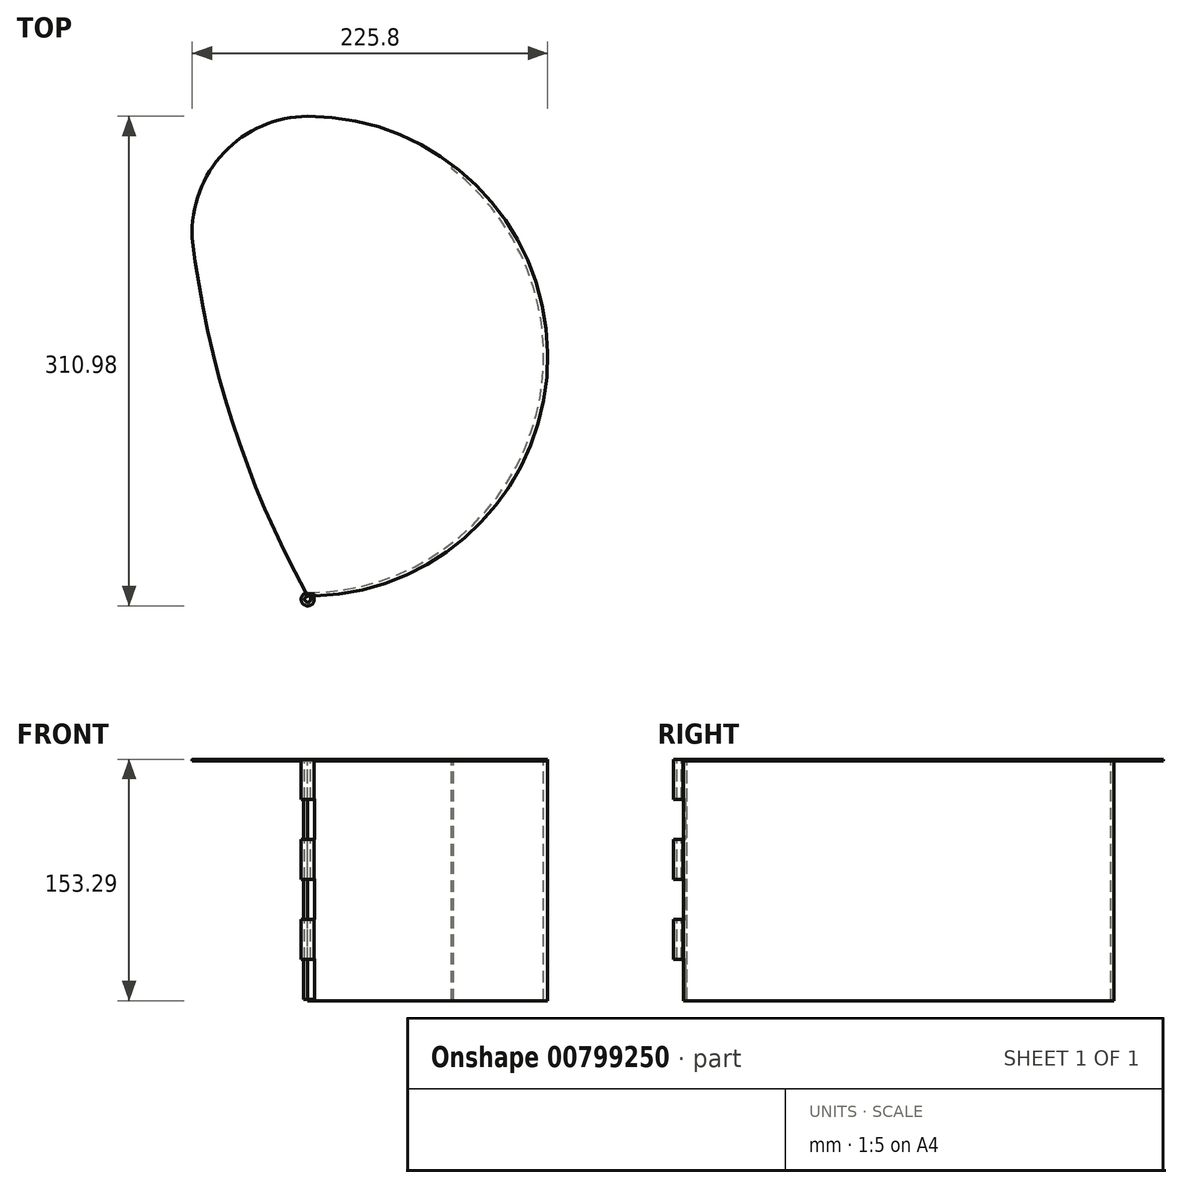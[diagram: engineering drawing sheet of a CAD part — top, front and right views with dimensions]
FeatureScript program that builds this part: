
annotation { "Feature Type Name" : "Feature", "Feature Type Description" : "" }
export const myFeature = defineFeature(function(context is Context, id is Id, definition is map)
    precondition{}
    {
        {
            var Q0;
            Q0=qCreatedBy(makeId("Top.planeOp"),FACE);
            var sketch = newSketch(context, id + "F0", { "sketchPlane" : qUnion([Q0])});
            skArc(sketch, "E0", {"start": v(-1.65, -152.87) * mm, "mid": v(150.75, -0.47) * mm, "end": v(-1.65, 151.93) * mm});
            skArc(sketch, "E1", {"start": v(-1.65, 151.93) * mm, "mid": v(-54.83, 128.83) * mm, "end": v(-74.97, 74.46) * mm});
            skArc(sketch, "E2", {"start": v(-74.97, 74.46) * mm, "mid": v(-49.39, -42.78) * mm, "end": v(-1.65, -152.87) * mm});
            skLineSegment(sketch, "E3", {"start": v(104.86, 103.41) * mm, "end": v(107.44, 105.95) * mm});
            skArc(sketch, "E4", {"start": v(-3.82, -148.92) * mm, "mid": v(134.5, -58.93) * mm, "end": v(104.86, 103.41) * mm});
            skSolve(sketch);
        }
        {
            var Q0;
            {var subQ2=sQuery(id+"F0.wireOp",EDGE,"E1");Q0=makeQuery(id+"F0.imprint","IMPRINT",FACE,{"disambiguationData":[TD([[makeQuery(id+"F0.imprint","IMPRINT",EDGE,{"derivedFrom":subQ2}),1.0]])]});}
            var Q1;
            {var subQ3=sQuery(id+"F0.wireOp",EDGE,"E3");Q1=makeQuery(id+"F0.imprint","IMPRINT",FACE,{"disambiguationData":[TD([[makeQuery(id+"F0.imprint","IMPRINT",EDGE,{"derivedFrom":subQ3}),-1.0]])]});}
            extrude(context, id + "F1", {"entities" : qUnion([Q0, Q1]), "depth" : 0.89 * mm, "offsetDistance" : 25.4 * mm});
        }
        {
            var Q0;
            Q0=makeQuery(id+"F1.opExtrude","CAP_FACE",FACE,{"disambiguationData":[OSD([sQuery(id+"F0.wireOp",EDGE,"E0"),sQuery(id+"F0.wireOp",EDGE,"E1"),sQuery(id+"F0.wireOp",EDGE,"E2")])],"isStart":true});
            var sketch = newSketch(context, id + "F2", { "sketchPlane" : qUnion([Q0])});
            skArc(sketch, "E5", {"start": v(90.86, -120.44) * mm, "mid": v(142.45, 49.33) * mm, "end": v(-1.65, 152.87) * mm});
            skLineSegment(sketch, "E6", {"start": v(-1.65, 152.87) * mm, "end": v(-1.65, 150.7) * mm});
            skLineSegment(sketch, "E7", {"start": v(89.6, -118.78) * mm, "end": v(90.96, -120.57) * mm});
            skArc(sketch, "E8", {"start": v(89.6, -118.78) * mm, "mid": v(140.28, 48.57) * mm, "end": v(-1.65, 150.7) * mm});
            skSolve(sketch);
        }
        {
            var Q0;
            Q0 = qSketchRegion(id + "F2", true);
            extrude(context, id + "F3", {"entities" : qUnion([Q0]), "operationType" : NewBodyOperationType.ADD, "depth" : 152.4 * mm, "offsetDistance" : 25.4 * mm});
        }
        {
            var Q0;
            Q0=makeQuery(id+"F1.opExtrude","CAP_FACE",FACE,{"disambiguationData":[OSD([sQuery(id+"F0.wireOp",EDGE,"E0"),sQuery(id+"F0.wireOp",EDGE,"E1"),sQuery(id+"F0.wireOp",EDGE,"E2")])],"isStart":false});
            var sketch = newSketch(context, id + "F4", { "sketchPlane" : qUnion([Q0])});
            skArc(sketch, "E9", {"start": v(-1.68, -152.97) * mm, "mid": v(-2.64, -156.5) * mm, "end": v(0.07, -154.05) * mm});
            skArc(sketch, "E10", {"start": v(-1.68, -150.7) * mm, "mid": v(-3.85, -158.42) * mm, "end": v(2.1, -153.06) * mm});
            skLineSegment(sketch, "E11", {"start": v(-1.68, -150.7) * mm, "end": v(-1.68, -152.97) * mm});
            skLineSegment(sketch, "E12", {"start": v(0.07, -154.05) * mm, "end": v(2.1, -153.06) * mm});
            skSolve(sketch);
        }
        {
            var Q0;
            {var subQ1=sQuery(id+"F4.wireOp",EDGE,"E9");Q0=makeQuery(id+"F4.imprint","IMPRINT",FACE,{"disambiguationData":[TD([[makeQuery(id+"F4.imprint","IMPRINT",EDGE,{"derivedFrom":subQ1}),-1.0]])]});}
            var Q1;
            {var subQ0=sQuery(id+"F4.wireOp",EDGE,"E11");var subQ1=sQuery(id+"F4.wireOp",EDGE,"E10");var subQ2=makeQuery(id+"F4.imprint","INTERSECT",VERTEX,{"derivedFrom":[subQ1,subQ0]});Q1=makeQuery(id+"F4.imprint","IMPRINT",FACE,{"disambiguationData":[TD([[makeQuery(id+"F4.imprint","IMPRINT",EDGE,{"disambiguationData":[TD([[subQ2,-1.0]])],"derivedFrom":subQ1}),1.0]])]});}
            extrude(context, id + "F5", {"entities" : qUnion([Q0, Q1]), "operationType" : NewBodyOperationType.ADD, "oppositeDirection" : true, "depth" : 152.4 * mm, "offsetDistance" : 25.4 * mm});
        }
        {
            var Q0;
            Q0=qCreatedBy(makeId("Right.planeOp"),FACE);
            var sketch = newSketch(context, id + "F6", { "sketchPlane" : qUnion([Q0])});
            skLineSegment(sketch, "E13", {"start": v(-151.56, 0.84) * mm, "end": v(-151.56, 9.5) * mm});
            skLineSegment(sketch, "E14", {"start": v(-151.56, 9.5) * mm, "end": v(-177.33, 9.5) * mm});
            skLineSegment(sketch, "E15", {"start": v(-177.33, 9.5) * mm, "end": v(-177.33, -151.56) * mm});
            skLineSegment(sketch, "E16", {"start": v(-177.33, -151.56) * mm, "end": v(-151.56, -151.56) * mm});
            skLineSegment(sketch, "E17", {"start": v(-151.56, -151.56) * mm, "end": v(-151.56, -126.16) * mm});
            skLineSegment(sketch, "E18", {"start": v(-151.56, -126.16) * mm, "end": v(-160.2, -126.16) * mm});
            skLineSegment(sketch, "E19", {"start": v(-160.2, -126.16) * mm, "end": v(-160.2, -100.76) * mm});
            skLineSegment(sketch, "E20", {"start": v(-160.2, -100.76) * mm, "end": v(-151.56, -100.76) * mm});
            skLineSegment(sketch, "E21", {"start": v(-151.56, -100.76) * mm, "end": v(-151.56, -75.36) * mm});
            skLineSegment(sketch, "E22", {"start": v(-151.56, -75.36) * mm, "end": v(-160.2, -75.36) * mm});
            skLineSegment(sketch, "E23", {"start": v(-160.2, -75.36) * mm, "end": v(-160.2, -49.96) * mm});
            skLineSegment(sketch, "E24", {"start": v(-160.2, -49.96) * mm, "end": v(-151.56, -49.96) * mm});
            skLineSegment(sketch, "E25", {"start": v(-151.56, -49.96) * mm, "end": v(-151.56, -24.56) * mm});
            skLineSegment(sketch, "E26", {"start": v(-151.56, -24.56) * mm, "end": v(-160.2, -24.56) * mm});
            skLineSegment(sketch, "E27", {"start": v(-160.2, -24.56) * mm, "end": v(-160.2, 0.84) * mm});
            skLineSegment(sketch, "E28", {"start": v(-160.2, 0.84) * mm, "end": v(-151.56, 0.84) * mm});
            skPoint(sketch, "E29.orphan", {"position": v(-151.56, 0) * mm});
            skSolve(sketch);
        }
        {
            var Q0;
            Q0=makeQuery(id+"F6.imprint","IMPRINT",FACE,{"disambiguationData":[TD([[makeQuery(id+"F6.imprint","IMPRINT",EDGE,{"derivedFrom":sQuery(id+"F6.wireOp",EDGE,"E13")}),1.0]])]});
            extrude(context, id + "F7", {"entities" : qUnion([Q0]), "operationType" : NewBodyOperationType.REMOVE, "depth" : 2.8 * mm, "offsetDistance" : 25.4 * mm, "hasSecondDirection" : true, "secondDirectionOppositeDirection" : true, "secondDirectionDepth" : 25.4 * mm});
        }
    });
